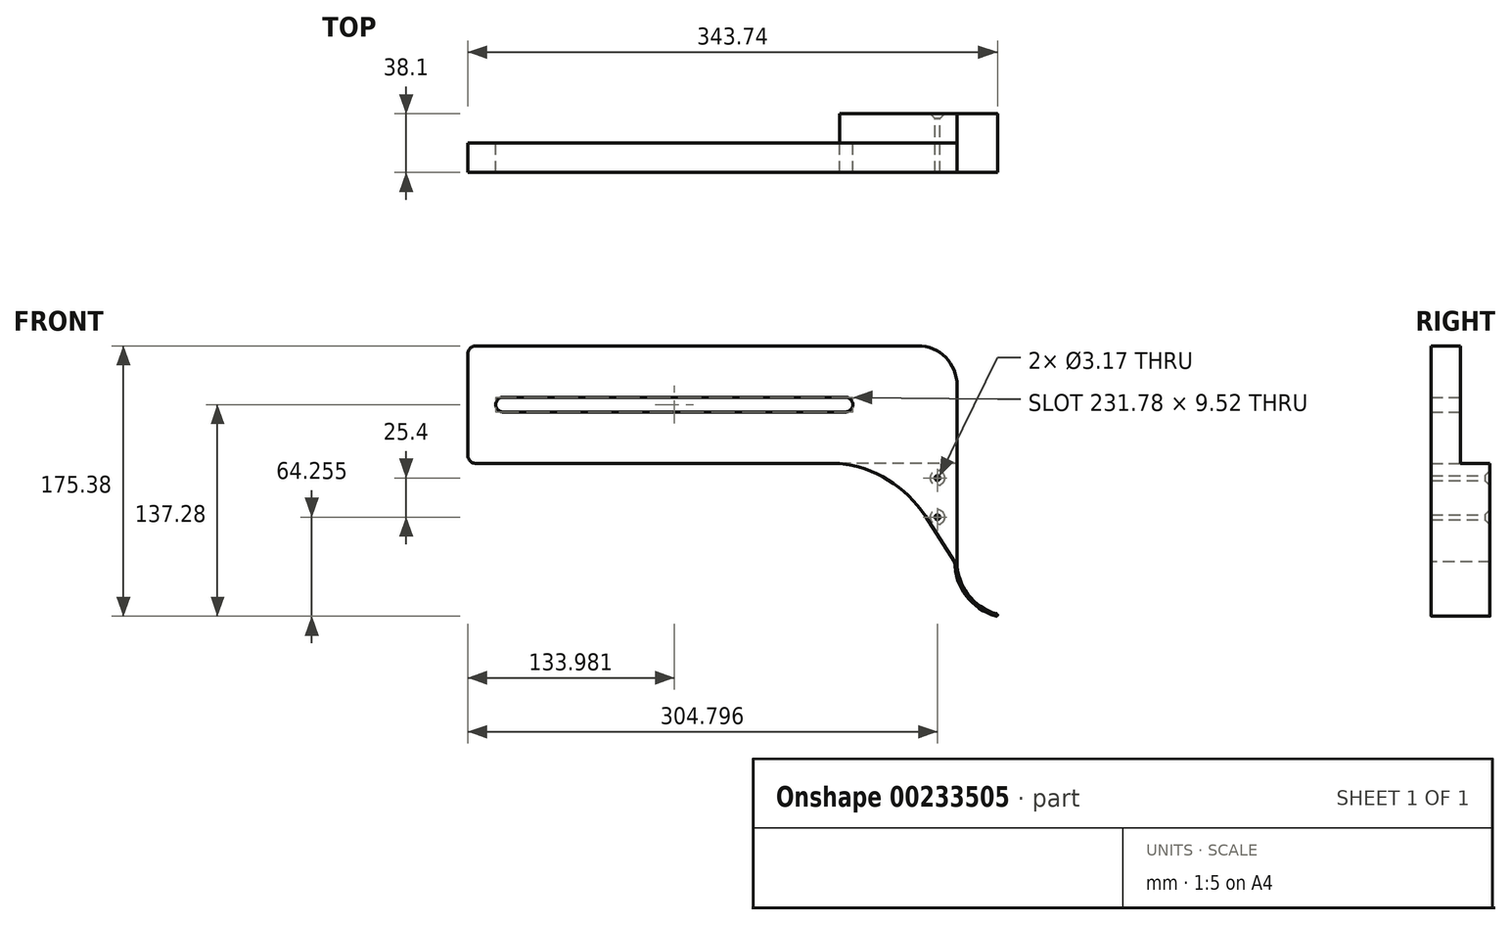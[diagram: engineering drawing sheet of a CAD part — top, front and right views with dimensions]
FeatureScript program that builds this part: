
annotation { "Feature Type Name" : "Feature", "Feature Type Description" : "" }
export const myFeature = defineFeature(function(context is Context, id is Id, definition is map)
    precondition{}
    {
        {
            var Q0;
            Q0=qCreatedBy(makeId("Front.planeOp"),FACE);
            var sketch = newSketch(context, id + "F0", { "sketchPlane" : qUnion([Q0])});
            skLineSegment(sketch, "E0", {"start": v(-166.64, 76.2) * mm, "end": v(150.86, 76.2) * mm});
            skLineSegment(sketch, "E1", {"start": v(150.86, 76.2) * mm, "end": v(150.86, -66.14) * mm});
            skLineSegment(sketch, "E2", {"start": v(-166.64, 76.2) * mm, "end": v(-166.64, 0) * mm});
            skLineSegment(sketch, "E3", {"start": v(-143.78, 33.34) * mm, "end": v(78.47, 33.34) * mm});
            skLineSegment(sketch, "E4", {"start": v(-143.78, 42.86) * mm, "end": v(78.47, 42.86) * mm});
            skArc(sketch, "E5", {"start": v(-143.78, 33.34) * mm, "mid": v(-148.55, 38.1) * mm, "end": v(-143.78, 42.86) * mm});
            skArc(sketch, "E6", {"start": v(78.47, 42.86) * mm, "mid": v(83.23, 38.1) * mm, "end": v(78.47, 33.34) * mm});
            skLineSegment(sketch, "E7", {"start": v(-166.64, 38.1) * mm, "end": v(150.86, 38.1) * mm, "construction": true});
            skCircle(sketch, "E8", {"center": v(138.16, -34.92) * mm, "radius": 1.4 * mm});
            skCircle(sketch, "E9", {"center": v(138.16, -9.52) * mm, "radius": 1.4 * mm});
            skLineSegment(sketch, "E10", {"start": v(-166.64, 0) * mm, "end": v(74.66, 0) * mm});
            skLineSegment(sketch, "E11", {"start": v(150.86, -66.14) * mm, "end": v(130.1, -34.19) * mm});
            skArc(sketch, "E12", {"start": v(130.1, -34.19) * mm, "mid": v(106.22, -10.86) * mm, "end": v(74.66, 0) * mm});
            skLineSegment(sketch, "E13", {"start": v(138.16, -34.92) * mm, "end": v(132.83, -38.38) * mm, "construction": true});
            skSolve(sketch);
        }
        {
            var Q0;
            Q0=makeQuery(id+"F0.imprint","IMPRINT",FACE,{"disambiguationData":[TD([[makeQuery(id+"F0.imprint","IMPRINT",EDGE,{"derivedFrom":sQuery(id+"F0.wireOp",EDGE,"E0")}),-1.0]])]});
            var Q1;
            Q1=makeQuery(id+"F0.imprint","IMPRINT",FACE,{"disambiguationData":[TD([[makeQuery(id+"F0.imprint","IMPRINT",EDGE,{"derivedFrom":sQuery(id+"F0.wireOp",EDGE,"E8")}),1.0]])]});
            var Q2;
            Q2=makeQuery(id+"F0.imprint","IMPRINT",FACE,{"disambiguationData":[TD([[makeQuery(id+"F0.imprint","IMPRINT",EDGE,{"derivedFrom":sQuery(id+"F0.wireOp",EDGE,"E9")}),1.0]])]});
            extrude(context, id + "F1", {"entities" : qUnion([Q0, Q1, Q2]), "depth" : 19.05 * mm});
        }
        {
            var Q0;
            Q0=makeQuery(id+"F1.opExtrude","SWEPT_EDGE",EDGE,{"disambiguationData":[OSD([sQuery(id+"F0.wireOp",EDGE,"E2"),sQuery(id+"F0.wireOp",EDGE,"7v6yTp73-L3JC-DiDH-DaO4-LWgb14ICGSQ6")])]});
            var Q1;
            Q1=makeQuery(id+"F1.opExtrude","SWEPT_EDGE",EDGE,{"disambiguationData":[OSD([sQuery(id+"F0.wireOp",EDGE,"E0"),sQuery(id+"F0.wireOp",EDGE,"E2")])]});
            fillet(context, id + "F2", {"entities" : qUnion([Q0, Q1]), "radius" : 5.08 * mm, "tangentPropagation" : true, "allowEdgeOverflow" : false});
        }
        {
            var Q0;
            Q0=makeQuery(id+"F1.opExtrude","SWEPT_EDGE",EDGE,{"disambiguationData":[OSD([sQuery(id+"F0.wireOp",EDGE,"E0"),sQuery(id+"F0.wireOp",EDGE,"E1")])]});
            fillet(context, id + "F3", {"entities" : qUnion([Q0]), "radius" : 25.4 * mm, "tangentPropagation" : true, "allowEdgeOverflow" : false});
        }
        {
            var Q0;
            Q0=makeQuery(id+"F1.opExtrude","CAP_FACE",FACE,{"disambiguationData":[OSD([sQuery(id+"F0.wireOp",EDGE,"E0"),sQuery(id+"F0.wireOp",EDGE,"E1"),sQuery(id+"F0.wireOp",EDGE,"E2"),sQuery(id+"F0.wireOp",EDGE,"E3"),sQuery(id+"F0.wireOp",EDGE,"E4"),sQuery(id+"F0.wireOp",EDGE,"E5"),sQuery(id+"F0.wireOp",EDGE,"E6"),sQuery(id+"F0.wireOp",EDGE,"E8"),sQuery(id+"F0.wireOp",EDGE,"E9"),sQuery(id+"F0.wireOp",EDGE,"E10"),sQuery(id+"F0.wireOp",EDGE,"E11"),sQuery(id+"F0.wireOp",EDGE,"E12")])],"isStart":true});
            var sketch = newSketch(context, id + "F4", { "sketchPlane" : qUnion([Q0])});
            skLineSegment(sketch, "E14", {"start": v(-150.86, -66.14) * mm, "end": v(-150.86, 0) * mm});
            skLineSegment(sketch, "E15", {"start": v(-150.86, 0) * mm, "end": v(-74.66, 0) * mm});
            skLineSegment(sketch, "E16", {"start": v(-150.86, -66.14) * mm, "end": v(-130.1, -34.19) * mm});
            skArc(sketch, "E17", {"start": v(-74.66, 0) * mm, "mid": v(-106.22, -10.86) * mm, "end": v(-130.1, -34.19) * mm});
            skCircle(sketch, "E18", {"center": v(-138.16, -34.92) * mm, "radius": 1.4 * mm});
            skCircle(sketch, "E19", {"center": v(-138.16, -9.52) * mm, "radius": 1.4 * mm});
            skSolve(sketch);
        }
        {
            var Q0;
            Q0=makeQuery(id+"F4.imprint","IMPRINT",FACE,{"disambiguationData":[TD([[makeQuery(id+"F4.imprint","IMPRINT",EDGE,{"derivedFrom":sQuery(id+"F4.wireOp",EDGE,"E14")}),1.0]])]});
            var Q1;
            Q1=makeQuery(id+"F4.imprint","IMPRINT",FACE,{"disambiguationData":[TD([[makeQuery(id+"F4.imprint","IMPRINT",EDGE,{"derivedFrom":sQuery(id+"F4.wireOp",EDGE,"E18")}),1.0]])]});
            var Q2;
            Q2=makeQuery(id+"F4.imprint","IMPRINT",FACE,{"disambiguationData":[TD([[makeQuery(id+"F4.imprint","IMPRINT",EDGE,{"derivedFrom":sQuery(id+"F4.wireOp",EDGE,"E19")}),1.0]])]});
            extrude(context, id + "F5", {"entities" : qUnion([Q0, Q1, Q2]), "operationType" : NewBodyOperationType.ADD, "depth" : 19.05 * mm});
        }
        {
            var Q0;
            Q0=makeQuery(id+"F5.opExtrude","CAP_FACE",FACE,{"disambiguationData":[OSD([sQuery(id+"F4.wireOp",EDGE,"E14"),sQuery(id+"F4.wireOp",EDGE,"E15"),sQuery(id+"F4.wireOp",EDGE,"E16"),sQuery(id+"F4.wireOp",EDGE,"E17")])],"isStart":false});
            var sketch = newSketch(context, id + "F6", { "sketchPlane" : qUnion([Q0])});
            skCircle(sketch, "E20", {"center": v(-138.16, -34.92) * mm, "radius": 1.4 * mm});
            skCircle(sketch, "E21", {"center": v(-138.16, -9.52) * mm, "radius": 1.4 * mm});
            skSolve(sketch);
        }
        {
            var Q0;
            Q0=sQuery(id+"F6.wireOp",VERTEX,"E20.center");
            var Q1;
            Q1=sQuery(id+"F6.wireOp",VERTEX,"E21.center");
            var Q2;
            Q2=makeQuery(id+"F1.opExtrude","SWEPT_BODY",BODY,{"disambiguationData":[OSD([sQuery(id+"F0.wireOp",EDGE,"E0"),sQuery(id+"F0.wireOp",EDGE,"E1"),sQuery(id+"F0.wireOp",EDGE,"E2"),sQuery(id+"F0.wireOp",EDGE,"E3"),sQuery(id+"F0.wireOp",EDGE,"E4"),sQuery(id+"F0.wireOp",EDGE,"E5"),sQuery(id+"F0.wireOp",EDGE,"E6"),sQuery(id+"F0.wireOp",EDGE,"E10"),sQuery(id+"F0.wireOp",EDGE,"E11"),sQuery(id+"F0.wireOp",EDGE,"E12")])]});
            var Q3;
            Q3=makeQuery(id+"F5.opExtrude","SWEPT_BODY",BODY,{"disambiguationData":[OSD([sQuery(id+"F4.wireOp",EDGE,"E14"),sQuery(id+"F4.wireOp",EDGE,"E15"),sQuery(id+"F4.wireOp",EDGE,"E16"),sQuery(id+"F4.wireOp",EDGE,"E17")])]});
            hole(context, id + "F7", {"style" : HoleStyle.C_SINK, "endStyle" : HoleEndStyle.THROUGH, "holeDiameter" : 3.17 * mm, "cSinkDiameter" : 9.52 * mm, "cSinkAngle" : 90 * degree, "locations" : qUnion([Q0, Q1]), "scope" : qUnion([Q2, Q3]), "isTappedThrough" : true});
        }
        {
            var Q0;
            Q0=makeQuery(id+"F1.opExtrude","CAP_FACE",FACE,{"disambiguationData":[OSD([sQuery(id+"F0.wireOp",EDGE,"E0"),sQuery(id+"F0.wireOp",EDGE,"E1"),sQuery(id+"F0.wireOp",EDGE,"E2"),sQuery(id+"F0.wireOp",EDGE,"E3"),sQuery(id+"F0.wireOp",EDGE,"E4"),sQuery(id+"F0.wireOp",EDGE,"E5"),sQuery(id+"F0.wireOp",EDGE,"E6"),sQuery(id+"F0.wireOp",EDGE,"E10"),sQuery(id+"F0.wireOp",EDGE,"E11"),sQuery(id+"F0.wireOp",EDGE,"E12")])],"isStart":false});
            var sketch = newSketch(context, id + "F8", { "sketchPlane" : qUnion([Q0])});
            skLineSegment(sketch, "E22", {"start": v(150.86, -2.64) * mm, "end": v(150.86, -66.14) * mm});
            skLineSegment(sketch, "E23", {"start": v(150.86, -2.64) * mm, "end": v(149.33, -2.64) * mm});
            skLineSegment(sketch, "E24", {"start": v(149.33, -2.64) * mm, "end": v(149.33, -66.14) * mm});
            skLineSegment(sketch, "E25", {"start": v(149.33, -66.14) * mm, "end": v(150.86, -66.14) * mm});
            skSolve(sketch);
        }
        {
            var Q0;
            {var subQ0=sQuery(id+"F8.wireOp",EDGE,"E22");Q0=makeQuery(id+"F8.imprint","IMPRINT",FACE,{"disambiguationData":[TD([[makeQuery(id+"F8.imprint","IMPRINT",EDGE,{"derivedFrom":subQ0}),-1.0]])]});}
            extrude(context, id + "F9", {"entities" : qUnion([Q0]), "operationType" : NewBodyOperationType.REMOVE, "endBound" : BoundingType.THROUGH_ALL, "oppositeDirection" : true, "depth" : 25.4 * mm});
        }
        {
            var Q0;
            Q0=qCreatedBy(makeId("Front.planeOp"),FACE);
            var sketch = newSketch(context, id + "F10", { "sketchPlane" : qUnion([Q0])});
            skLineSegment(sketch, "E26", {"start": v(150.86, -2.64) * mm, "end": v(150.86, -63.8) * mm});
            skLineSegment(sketch, "E27", {"start": v(150.86, -2.64) * mm, "end": v(149.33, -2.64) * mm});
            skLineSegment(sketch, "E28", {"start": v(149.33, -2.64) * mm, "end": v(149.33, -63.8) * mm});
            skArc(sketch, "E29", {"start": v(149.33, -63.8) * mm, "mid": v(156.79, -85.98) * mm, "end": v(176.13, -99.15) * mm});
            skArc(sketch, "E30.0", {"start": v(150.86, -63.8) * mm, "mid": v(158, -85.06) * mm, "end": v(176.54, -97.69) * mm});
            skArc(sketch, "E31", {"start": v(176.13, -99.15) * mm, "mid": v(177.07, -98.63) * mm, "end": v(176.54, -97.69) * mm});
            skSolve(sketch);
        }
        {
            var Q0;
            Q0=makeQuery(id+"F10.imprint","IMPRINT",FACE,{"disambiguationData":[TD([[makeQuery(id+"F10.imprint","IMPRINT",EDGE,{"derivedFrom":sQuery(id+"F10.wireOp",EDGE,"E26")}),-1.0]])]});
            extrude(context, id + "F11", {"entities" : qUnion([Q0]), "operationType" : NewBodyOperationType.ADD, "depth" : 19.05 * mm, "hasSecondDirection" : true, "secondDirectionOppositeDirection" : true, "secondDirectionDepth" : 19.05 * mm});
        }
    });
